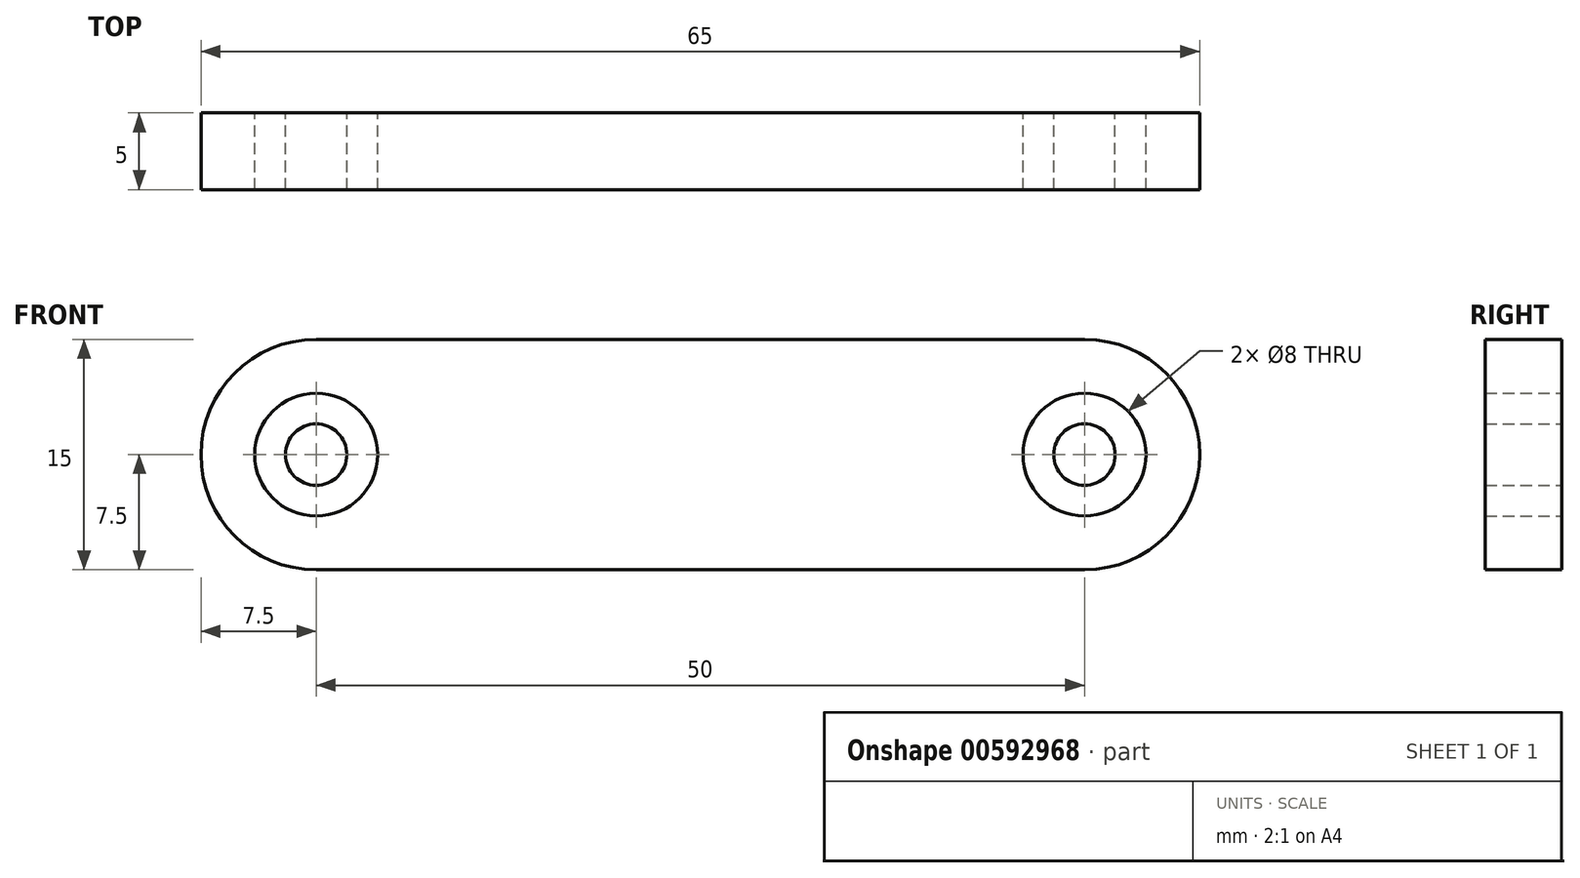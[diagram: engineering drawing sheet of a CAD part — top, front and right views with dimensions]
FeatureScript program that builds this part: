
annotation { "Feature Type Name" : "Feature", "Feature Type Description" : "" }
export const myFeature = defineFeature(function(context is Context, id is Id, definition is map)
    precondition{}
    {
        {
            var Q0;
            Q0=qCreatedBy(makeId("Front.planeOp"),FACE);
            var sketch = newSketch(context, id + "F0", { "sketchPlane" : qUnion([Q0])});
            skArc(sketch, "E0", {"start": v(0, 7.5) * mm, "mid": v(-7.5, 0) * mm, "end": v(0, -7.5) * mm});
            skCircle(sketch, "E1", {"center": v(0, 0) * mm, "radius": 4 * mm});
            skArc(sketch, "E2", {"start": v(50, -7.5) * mm, "mid": v(57.5, 0) * mm, "end": v(50, 7.5) * mm});
            skCircle(sketch, "E3", {"center": v(50, 0) * mm, "radius": 4 * mm});
            skCircle(sketch, "E4", {"center": v(50, 0) * mm, "radius": 2 * mm});
            skCircle(sketch, "E5", {"center": v(0, 0) * mm, "radius": 2 * mm});
            skLineSegment(sketch, "E6", {"start": v(0, 7.5) * mm, "end": v(50, 7.5) * mm});
            skLineSegment(sketch, "E7", {"start": v(0, -7.5) * mm, "end": v(50, -7.5) * mm});
            skSolve(sketch);
        }
        {
            var Q0;
            Q0=makeQuery(id+"F0.imprint","IMPRINT",FACE,{"disambiguationData":[TD([[makeQuery(id+"F0.imprint","IMPRINT",EDGE,{"derivedFrom":sQuery(id+"F0.wireOp",EDGE,"E0")}),1.0]])]});
            var Q1;
            Q1=makeQuery(id+"F0.imprint","IMPRINT",FACE,{"disambiguationData":[TD([[makeQuery(id+"F0.imprint","IMPRINT",EDGE,{"derivedFrom":sQuery(id+"F0.wireOp",EDGE,"E5")}),1.0]])]});
            var Q2;
            Q2=makeQuery(id+"F0.imprint","IMPRINT",FACE,{"disambiguationData":[TD([[makeQuery(id+"F0.imprint","IMPRINT",EDGE,{"derivedFrom":sQuery(id+"F0.wireOp",EDGE,"E4")}),1.0]])]});
            extrude(context, id + "F1", {"entities" : qUnion([Q0, Q1, Q2]), "depth" : 5 * mm, "offsetDistance" : 25 * mm});
        }
    });
